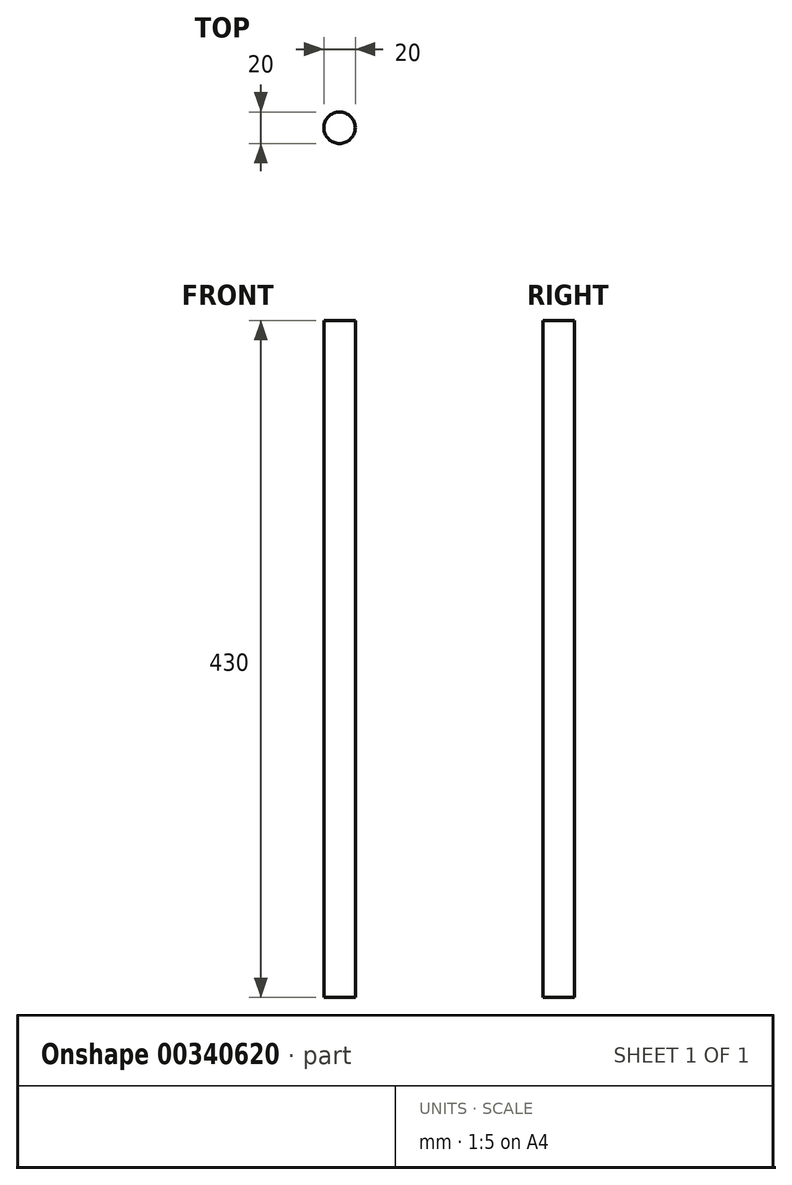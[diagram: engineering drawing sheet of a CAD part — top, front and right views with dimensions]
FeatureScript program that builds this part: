
annotation { "Feature Type Name" : "Feature", "Feature Type Description" : "" }
export const myFeature = defineFeature(function(context is Context, id is Id, definition is map)
    precondition{}
    {
        {
            var Q0;
            Q0=qCreatedBy(makeId("Top.planeOp"),FACE);
            var sketch = newSketch(context, id + "F0", { "sketchPlane" : qUnion([Q0])});
            skCircle(sketch, "E0", {"center": v(0, 0) * mm, "radius": 10 * mm});
            skSolve(sketch);
        }
        {
            var Q0;
            Q0 = qSketchRegion(id + "F0", true);
            extrude(context, id + "F1", {"entities" : qUnion([Q0]), "depth" : 430 * mm});
        }
    });
